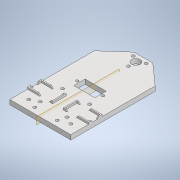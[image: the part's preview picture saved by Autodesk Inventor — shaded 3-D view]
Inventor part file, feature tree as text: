
AUTODESK INVENTOR PART (.ipt)
format: ipt  version: 2020 (Build 240168000, 168)  size: 423,424 bytes
history: native  units: mm
features: extrude x8, sketch x8, chamfer x1, plane x1, mirror x1, hole x1, fillet x1, projected_geometry x1
ambient origin geometry x8: Origin, YZ Plane, XZ Plane, XY Plane, X Axis, Y Axis, Z Axis, Center Point
bodies: Solid1 (feature_tree)
feature tree (22):
  extrude  "Extrusion1"  Depth=80.0mm
  extrude  "Extrusion2"  Depth=20.0mm
  chamfer  "Chamfer1"  Distance=5.0mm
  plane  "Work Plane1"
  extrude  "Extrusion3"  Depth=12.2mm
  mirror  "Mirror1"
  sketch  "Sketch4"  dims[d8=24.4mm d9=20.0mm]
  extrude  "Extrusion4"  Depth=20.0mm
  extrude  "Extrusion5"  Depth=5.0mm
  extrude  "Extrusion6"  Depth=2.0mm TaperAngle=45.0deg
  extrude  "Extrusion7"  Depth=10.0mm
  hole  "Hole1"  [1 undecoded]
  fillet  "Fillet1"  [1 undecoded]
  extrude  "Extrusion8"  Depth=9.0mm
  sketch  "Sketch1"  dims[d0=65.0mm d1=80.0mm]
  sketch  "Sketch2"  dims[d2=20.0mm d3=20.0mm d4=5.0mm d5=0.0mm]
  sketch  "Sketch3"  dims[d6=1.2mm d7=12.2mm]
  sketch  "Sketch5"  dims[d10=2.0mm d11=0.0mm d12=5.0mm]
  sketch  "Sketch7"  dims[d13=5.0mm d14=2.0mm d15=2.0mm d16=45.0deg]
  sketch  "Sketch8"  dims[d17=10.0mm d19=2.5mm]
  sketch  "Sketch12"  dims[d20=24.0mm d21=3.4mm d22=0.0mm d23=0.0mm d24=9.0mm d25=13.856mm d26=3.3mm d27=8.0mm d28=0.0mm d29=0.0mm d30=53.0mm d31=22.7mm d32=12.2mm d33=13.75mm d34=13.75mm d35=3.0mm d36=0.0mm d37=0.0mm d38=3.3mm d40=24.0mm d41=0.0mm d42=0.0mm d43=10.0mm d44=3.3mm d45=50.0mm d46=0.0mm d47=0.0mm d48=45.0mm d49=52.0mm d50=29.0mm d51=3.0mm d52=6.0mm d53=5.4mm d54=2.3mm d55=90.0deg d56=8.0mm d57=20.594885mm d66=9.0mm d67=9.0mm d68=12.0mm d69=12.0mm d71=12.0mm d72=3.0mm d73=9.0mm d74=11.0mm d75=10.0mm d76=10.0mm d77=20.0mm d78=6.0mm d79=5.0mm d80=5.0mm d81=0.0mm d82=0.0mm]
  projected_geometry  "Projected Loop2"
note: 2 required parameter values undecoded (feature->parameter linkage not recoverable at this tier; creation-order binding heuristic only, values carry confidence <= 0.55)
